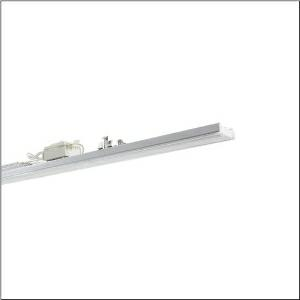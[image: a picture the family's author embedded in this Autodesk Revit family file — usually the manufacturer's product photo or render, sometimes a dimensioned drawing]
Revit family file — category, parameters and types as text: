
# Revit family: licross_21_recessed_mo_52te12dv4fxg3s4
name_source: partatom
category: Lighting Fixtures
units: mm (PartAtom-declared; Revit-internal decimal feet)

## family parameters
Cut with Voids When Loaded = No
Host = Face
Light Source = No
Part Type = Normal
Room Calculation Point = No
Round Connector Dimension = Use Diameter
Shared = No

## types (1)
- --- (1 x LED, 950 lm, 5.5 W, 4000K)
    Apparent Load = 6 VA
    CIE Flux Codes = 72 92 99 100 100
    Color Rendering = 80
    Color Temperature = 4000K
    Default Elevation = 1800 mm
    Description = Licross 21 Recessed MO, luminaire insert, of sheet steel, galvanised, coil coated, white, length: 2.250mm, width: 66mm, height: 67mm, LED rated luminous flux: 15.420lm, light colour: 840, SDCM (Standard Deviation of Colour Matching)MacAdam ≤ 3 SDCM (initial), control gear: DALI 2, with plug, 6-pole, with phase selection, for trunking rail, 9 or 11-core, mains connection: 220..240V, AC, 50/60Hz, rated input power: 89W, for trunking rail, 9-/11-core, internal wiring halogen-free, for emergency light function, converter,control gear: single battery element, battery: LiFePO4, 9Ah, primary optical cover: cover, of PMMA, light emission: direct distribution, primary light characteristic: symmetric, protection rating (complete): IP54, insulation class (complete): insulation class I (protective earthing), certification: CE, UKCA, protection symbol: D if used in an environment with non-conductive dust loads with corresponding accessories, impact resistance: IK06, permissible ambient temperature for indoor applications: +5..+35°C, standard: EN 60598-2-22, LABS conformity tested according to VDMA 24364:2018-05, reducing of maximum allowable ambient temperature of 5°C with ceiling mounting, corresponds to IFS (International Featured Standards) requirements for safety and quality in the food industry, The light source and the operating device comply with the requirements of the Ecodesign Regulation (EU) 2019/2020 and are replaceable in accordance with this regulation, packaging unit: 1 piece
    Height = 58 mm
    Lamp = 1 x LED
    Lamp Light Flux = 950 lm
    Lamp Power = 5.5 W
    Lamp count = 1
    Length = 2250 mm
    Luminous efficacy = 173 lm/W
    Manufacturer = Siteco
    ModVariant = No
    Model = 52TE12DV4FXG3S4
    Mounting Place = Ceiling
    Mounting Type = Pendant
    Number of Poles = 1
    OnlyDefault = Yes
    Power Factor = 1
    Product Name = Licross 21 Recessed MO
    Product group = luminaire insert | ceiling pendant
    ProductGroupID = 901
    Protection Class = Protection class I
    Protection Degree = IP 54
    RLX_Detail_Level = 1
    RLX_Emergency_Light_Flux = 0 lm
    RLX_Emergency_Type = 0
    RLX_Emergency_Type_DB = No
    RlxData = <blob elided: 30285 chars, md5=517ea479>
    Socket = socket
    Standby Power = 0 W
    System Light Flux = 950 lm
    System Power = 6 W
    Type Comments = : emergency light operation: 3 h
    Type Image = l_1296930.jpg
    URL = http://relux.com
    VarID = @adj_110009
    Voltage = 0 V
    Weight = 0.00 kg
    Width = 66 mm

## geometry (parser evidence)
native form markers: Blend x4, Sweep x11
no freeform markers — native parametric forms only
